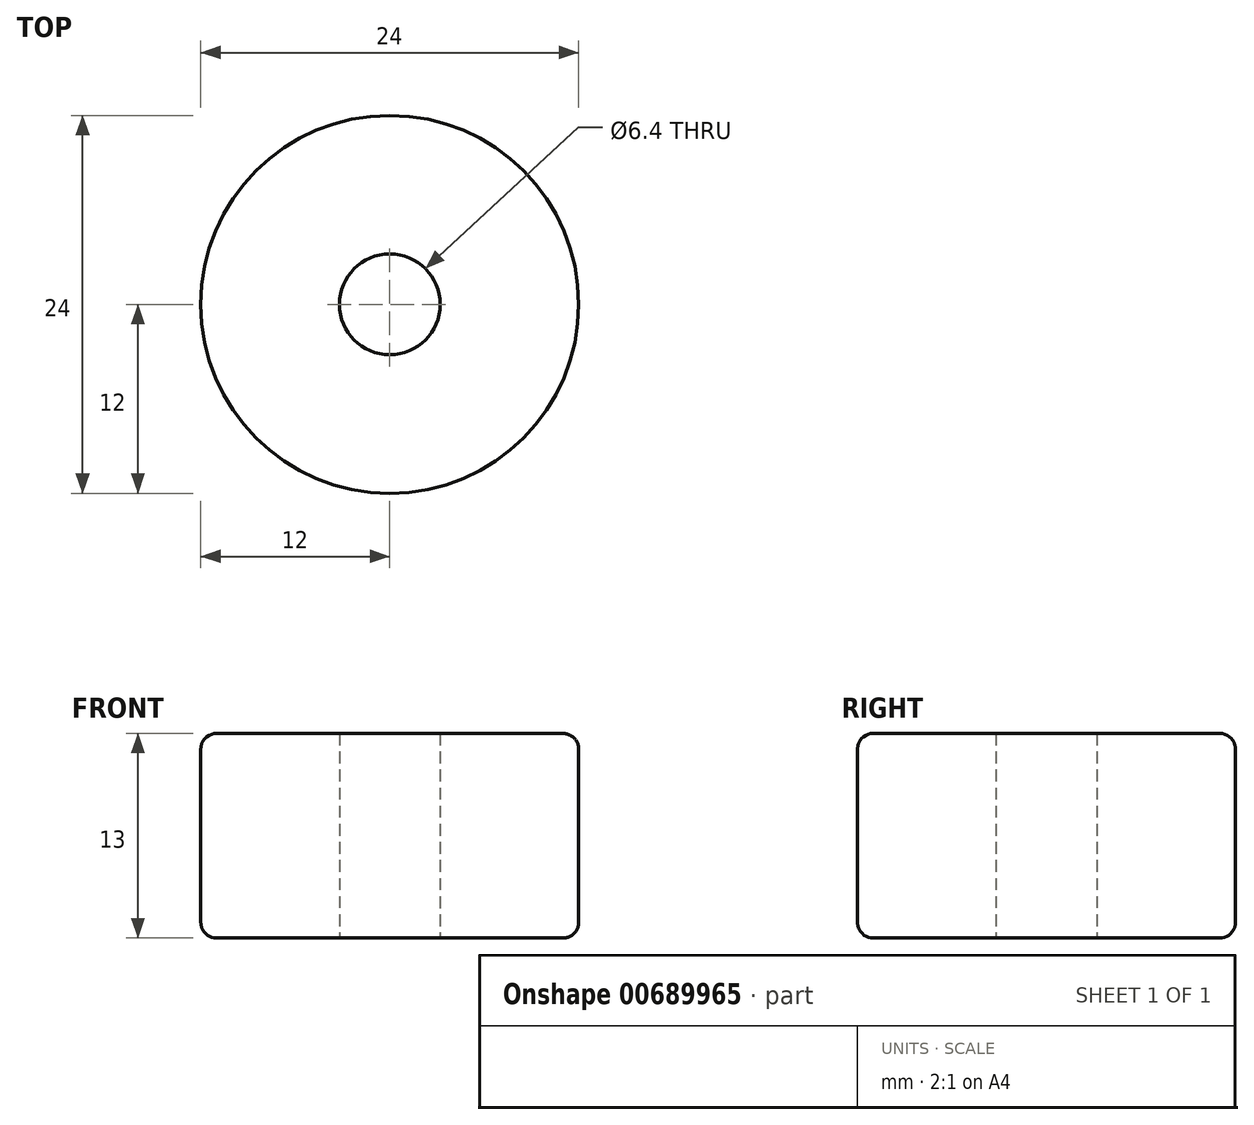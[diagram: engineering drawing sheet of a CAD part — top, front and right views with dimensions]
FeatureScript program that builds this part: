
annotation { "Feature Type Name" : "Feature", "Feature Type Description" : "" }
export const myFeature = defineFeature(function(context is Context, id is Id, definition is map)
    precondition{}
    {
        {
            var Q0;
            Q0=qCreatedBy(makeId("Top.planeOp"),FACE);
            var sketch = newSketch(context, id + "F0", { "sketchPlane" : qUnion([Q0])});
            skCircle(sketch, "E0", {"center": v(0, 0) * mm, "radius": 3.2 * mm});
            skPoint(sketch, "E1", {"position": v(0, 12) * mm});
            skPoint(sketch, "E2", {"position": v(-8.25, 0) * mm});
            skCircle(sketch, "E3", {"center": v(0, 0) * mm, "radius": 12 * mm});
            skSolve(sketch);
        }
        {
            var Q0;
            Q0=makeQuery(id+"F0.imprint","IMPRINT",FACE,{"disambiguationData":[TD([[makeQuery(id+"F0.imprint","IMPRINT",EDGE,{"derivedFrom":sQuery(id+"F0.wireOp",EDGE,"E0")}),-1.0]])]});
            extrude(context, id + "F1", {"entities" : qUnion([Q0]), "depth" : 13 * mm, "offsetDistance" : 25 * mm});
        }
        {
            var Q0;
            Q0=makeQuery(id+"F1.opExtrude","CAP_EDGE",EDGE,{"disambiguationData":[OSD([sQuery(id+"F0.wireOp",EDGE,"E3")])],"isStart":false});
            var Q1;
            Q1=makeQuery(id+"F1.opExtrude","CAP_EDGE",EDGE,{"disambiguationData":[OSD([sQuery(id+"F0.wireOp",EDGE,"E3")])],"isStart":true});
            fillet(context, id + "F2", {"entities" : qUnion([Q0, Q1]), "radius" : 1 * mm, "tangentPropagation" : true, "allowEdgeOverflow" : false});
        }
    });
